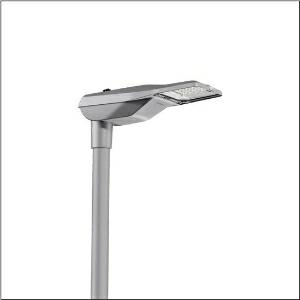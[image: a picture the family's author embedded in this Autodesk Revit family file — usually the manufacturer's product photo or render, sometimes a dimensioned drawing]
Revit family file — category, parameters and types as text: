
# Revit family: streetlight_sl_21_micro___p0_8ab_5xe1r33s08db_200d
name_source: partatom
category: Lighting Fixtures
units: mm (PartAtom-declared; Revit-internal decimal feet)

## family parameters
Cut with Voids When Loaded = No
Host = Face
Light Source = No
Part Type = Normal
Room Calculation Point = No
Round Connector Dimension = Use Diameter
Shared = No

## types (1)
- --- (1 x LED, 4470 lm, 39.1 W, 3000K)
    Apparent Load = 39 VA
    CIE Flux Codes = 36 71 98 100 100
    Color Rendering = 70
    Color Temperature = 3000K
    Default Elevation = 1800 mm
    Description = Streetlight SL 21 micro, mast luminaire, primary light control with lens, of PMMA, primary optical cover: cover, of toughened safety glass, transparent, light distribution: P0.8aB, light emission: direct distribution, primary light characteristic: asymmetric, installation type: post-top, side-entry, LED, High Power LED, rated luminous flux: 4.470lm, luminous efficacy: 114lm/W, light colour: 730, colour temperature: 3000K, control gear: D4i, control: pre-setting: logarithmic dimming characteristic, flexible luminous flux parameterisation, time-dependent luminous flux control, constant luminous flux control, overheat protection, mains connection: 220..240V, AC, 50/60Hz, start of lifetime: 39W, end of service life: 41W, reduction: 18W, luminaire housing, of diecast aluminium, powder-coated, SITECO metallic grey (DB 702S), corrosivity category C5 high according to DIN EN ISO 12944, multi-level sealing system, sealing non-destructively replaceable, inclination adjustable: 0°, 5°, 10°, 15°, please order mast flange separately, length: 528mm, width: 235mm, height: 110mm, mast flange for spigot size: 42mm (side-entry): 5XC10008XM4, 60/48mm (side-entry/post-top): 5XC10108XM2, 76/60mm (side-entry/post-top): 5XC10108XM1, Smart Interface above, protection rating (complete): IP66, insulation class (complete): insulation class II (safety insulation), certification: CE, ENEC, ENEC+, VDE, impact resistance: IK10, permissible operating ambient temperature for outdoor applications: -40..+50°C, standard-compliant lighting for roads and squares, packaging unit: 1 piece

Light Distribution: P0.8aB
    Height = 110 mm
    Lamp = 1 x LED
    Lamp Light Flux = 4470 lm
    Lamp Power = 39.1 W
    Lamp count = 1
    Length = 528 mm
    Luminous efficacy = 114 lm/W
    Manufacturer = Siteco
    ModVariant = No
    Model = 5XE1R33S08DB
    Number of Poles = 1
    OnlyDefault = Yes
    Power Factor = 1
    Product Name = Streetlight SL 21 micro | P0.8aB
    Product group = mast luminaire | pylon top
    ProductGroupID = 6100
    Protection Class = Protection class II
    Protection Degree = IP 66
    RLX_Detail_Level = 1
    RLX_Emergency_Light_Flux = 0 lm
    RLX_Emergency_Type = 0
    RLX_Emergency_Type_DB = No
    RlxData = <blob elided: 98425 chars, md5=5a48f03a>
    Socket = socket
    Standby Power = 0 W
    System Light Flux = 4470 lm
    System Power = 39 W
    Type Comments = factory setting: luminous flux: 100 % | dim-lin: 254 | 765 mA
    Type Image = l_1277292.jpg
    URL = http://relux.com
    VarID = @adj_082861
    Voltage = 0 V
    Weight = 0.00 kg
    Width = 235 mm

## geometry (parser evidence)
native form markers: Blend x4, Sweep x11
no freeform markers — native parametric forms only
